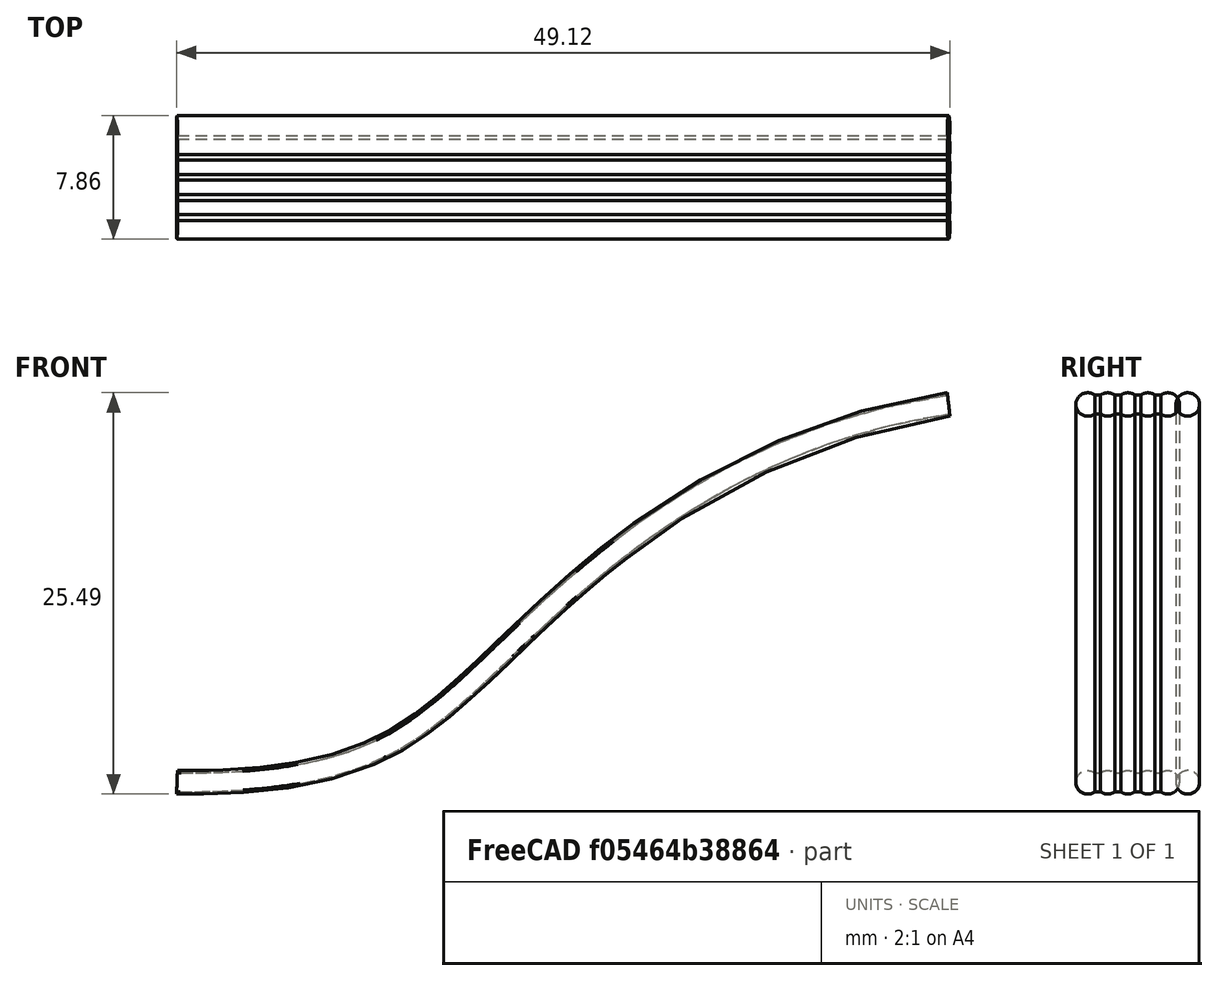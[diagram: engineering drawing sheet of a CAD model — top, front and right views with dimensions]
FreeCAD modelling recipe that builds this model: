
FCSTD DOCUMENT  (FreeCAD 0.20R29603 (Git))
Label: idc
License: All rights reserved
LicenseURL: https://en.wikipedia.org/wiki/All_rights_reserved
objects: Sketcher::SketchObject×4, Part::Sweep×2, App::VRMLObject×2, App::Part×2
note: 6 computed .brp shape members not serialized (recipe doc carries the construction recipe); baked Part::Feature solids carry a one-line shape summary decoded from their .brp

FEATURE [Sketcher::SketchObject] Sketch003
  FullyConstrained = false
  MapMode = 5
  Placement = pos=(0,0,0) rot=(1,0,0;1.5708rad)
  sketch-geometry (11):
    g0-g5: Circle x6 (B-spline internal-alignment scaffolding for g6; pole/knot coordinates omitted)
    g6: BSplineCurve PolesCount=6 KnotsCount=4 Degree=3 IsPeriodic=0
    g7-g10: GeomPoint x4 (B-spline internal-alignment scaffolding for g6; pole/knot coordinates omitted)
  constraints (11):
    c: Weight(g0) = 1
    c: PointOnObject(g6,g-1)
    c: Equal(g0,g1)
    c: PointOnObject(g1,g-2)
    c: Equal(g0,g2)
    c: PointOnObject(g2,g-1)
    c: Equal(g0,g3)
    c: Equal(g0,g4)
    c: Equal(g0,g5)
    c: InternalAlignment(g0-g5 -> g6) x6
    c: InternalAlignment(g7-g10 -> g6) x4
FEATURE [Sketcher::SketchObject] Sketch
  FullyConstrained = false
  MapMode = 5
  Placement = pos=(0,0,0) rot=(0.57735,0.57735,0.57735;2.0944rad)
  sketch-geometry (23):
    g0: LineSegment StartX=0 StartY=0 StartZ=0 EndX=1.27335 EndY=0 EndZ=0
    g1: LineSegment StartX=0 StartY=0 StartZ=0 EndX=1.27103 EndY=0 EndZ=0
    g2: LineSegment StartX=1.27103 StartY=0 StartZ=0 EndX=2.54207 EndY=0 EndZ=0
    g3: LineSegment StartX=2.54207 StartY=0 StartZ=0 EndX=3.8131 EndY=0 EndZ=0
    g4: LineSegment StartX=3.8131 StartY=0 StartZ=0 EndX=5.08414 EndY=0 EndZ=0
    g5: LineSegment StartX=0.45 StartY=0.6 StartZ=0 EndX=0.821034 EndY=0.6 EndZ=0
    g6: LineSegment StartX=0.45 StartY=-0.6 StartZ=0 EndX=0.821034 EndY=-0.6 EndZ=0
    g7: ArcOfCircle CenterX=5.08414 CenterY=7.1e-15 CenterZ=0 NormalX=0 NormalY=0 NormalZ=1 AngleXU=0 Radius=0.75 StartAngle=4.06889 EndAngle=5.35589
    g8: ArcOfCircle CenterX=3.8131 CenterY=0 CenterZ=0 NormalX=0 NormalY=0 NormalZ=1 AngleXU=0 Radius=0.75 StartAngle=4.06889 EndAngle=5.35589
    g9: ArcOfCircle CenterX=2.54207 CenterY=0 CenterZ=0 NormalX=0 NormalY=0 NormalZ=1 AngleXU=0 Radius=0.75 StartAngle=4.06889 EndAngle=5.35589
    g10: ArcOfCircle CenterX=1.27103 CenterY=-2e-16 CenterZ=0 NormalX=0 NormalY=0 NormalZ=1 AngleXU=0 Radius=0.75 StartAngle=4.06889 EndAngle=5.35589
    g11: ArcOfCircle CenterX=0 CenterY=-1e-16 CenterZ=0 NormalX=0 NormalY=0 NormalZ=1 AngleXU=0 Radius=0.75 StartAngle=0.927295 EndAngle=5.35589
    g12: ArcOfCircle CenterX=1.27103 CenterY=0 CenterZ=0 NormalX=0 NormalY=0 NormalZ=1 AngleXU=0 Radius=0.75 StartAngle=0.927295 EndAngle=2.2143
    g13: ArcOfCircle CenterX=2.54207 CenterY=0 CenterZ=0 NormalX=0 NormalY=0 NormalZ=1 AngleXU=0 Radius=0.75 StartAngle=0.927295 EndAngle=2.2143
    g14: ArcOfCircle CenterX=3.8131 CenterY=0 CenterZ=0 NormalX=0 NormalY=0 NormalZ=1 AngleXU=0 Radius=0.75 StartAngle=0.927295 EndAngle=2.2143
    g15: ArcOfCircle CenterX=5.08414 CenterY=-9.81007e-08 CenterZ=0 NormalX=0 NormalY=0 NormalZ=1 AngleXU=0 Radius=0.75 StartAngle=0.927295 EndAngle=2.2143
    g16: LineSegment StartX=4.2631 StartY=0.6 StartZ=0 EndX=4.63414 EndY=0.6 EndZ=0
    g17: LineSegment StartX=2.99207 StartY=0.6 StartZ=0 EndX=3.3631 EndY=0.6 EndZ=0
    g18: LineSegment StartX=1.72103 StartY=0.6 StartZ=0 EndX=2.09207 EndY=0.6 EndZ=0
    g19: LineSegment StartX=1.72103 StartY=-0.6 StartZ=0 EndX=2.09207 EndY=-0.6 EndZ=0
    g20: LineSegment StartX=2.99207 StartY=-0.6 StartZ=0 EndX=3.3631 EndY=-0.6 EndZ=0
    g21: LineSegment StartX=4.2631 StartY=-0.6 StartZ=0 EndX=4.63414 EndY=-0.6 EndZ=0
    g22: ArcOfCircle CenterX=5.08414 CenterY=7.1e-15 CenterZ=0 NormalX=0 NormalY=0 NormalZ=1 AngleXU=0 Radius=0.75 StartAngle=5.35589 EndAngle=7.21048
  constraints (36):
    c: Angle(g0) = 0
    c: Distance(g1) = 1.27103
    c: Angle(g1) = 0
    c: Equal(g1,g2)
    c: Parallel(g2,g1)
    c: Equal(g1,g3)
    c: Parallel(g3,g1)
    c: Equal(g1,g4)
    c: Parallel(g4,g1)
    c: Horizontal(g5)
    c: Horizontal(g6)
    c: PointOnObject(g7,g6)
    c: PointOnObject(g7,g6)
    c: PointOnObject(g8,g6)
    c: PointOnObject(g8,g6)
    c: PointOnObject(g9,g6)
    c: PointOnObject(g9,g6)
    c: Coincident(g6,g11)
    c: Coincident(g11,g5)
    c: Coincident(g16,g15)
    c: Coincident(g17,g14)
    c: Coincident(g16,g14)
    c: Coincident(g18,g13)
    c: Coincident(g17,g13)
    c: Coincident(g5,g12)
    c: Coincident(g18,g12)
    c: Coincident(g6,g10)
    c: Coincident(g19,g10)
    c: PointOnObject(g19,g9)
    c: PointOnObject(g20,g9)
    c: PointOnObject(g20,g8)
    c: PointOnObject(g21,g8)
    c: PointOnObject(g21,g7)
    c: Coincident(g22,g7)
    c: Coincident(g22,g15)
    c: Coincident(g22,g7)
FEATURE [Part::Sweep] Sweep
  Frenet = false
  Sections = -> [Sketch]
  Solid = false
  Spine = -> Sketch003 [Edge1]
  Transition = 1
FEATURE [App::VRMLObject] _90157000672001  label="690157000672001"
FEATURE [App::Part] Part
  Group = -> [_90157000672001]
  Origin = -> Origin
  Placement = pos=(-1.5e-15,3.25,0.5) rot=(0.707107,0.707107,0;3.14159rad)
FEATURE [Sketcher::SketchObject] Sketch005
  FullyConstrained = false
  MapMode = 5
  Placement = pos=(0,0,0) rot=(0.57735,0.57735,0.57735;2.0944rad)
  sketch-geometry (2):
    g0: ArcOfCircle CenterX=6.35517 CenterY=-2.69756e-08 CenterZ=0 NormalX=0 NormalY=0 NormalZ=1 AngleXU=0 Radius=0.75 StartAngle=4.06889 EndAngle=8.49748
    g1: ArcOfCircle CenterX=6.35517 CenterY=-2.69756e-08 CenterZ=0 NormalX=0 NormalY=0 NormalZ=1 AngleXU=0 Radius=0.75 StartAngle=2.2143 EndAngle=4.06889
  constraints (4):
    c: Radius(g0) = 0.75
    c: Coincident(g1,g0)
    c: Coincident(g1,g0)
    c: Coincident(g1,g0)
FEATURE [Sketcher::SketchObject] Sketch006
  FullyConstrained = false
  MapMode = 5
  Placement = pos=(0,0,0) rot=(1,0,0;1.5708rad)
  sketch-geometry (11):
    g0-g5: Circle x6 (B-spline internal-alignment scaffolding for g6; pole/knot coordinates omitted)
    g6: BSplineCurve PolesCount=6 KnotsCount=4 Degree=3 IsPeriodic=0
    g7-g10: GeomPoint x4 (B-spline internal-alignment scaffolding for g6; pole/knot coordinates omitted)
  constraints (11):
    c: Weight(g0) = 1
    c: PointOnObject(g6,g-1)
    c: Equal(g0,g1)
    c: PointOnObject(g1,g-2)
    c: Equal(g0,g2)
    c: PointOnObject(g2,g-1)
    c: Equal(g0,g3)
    c: Equal(g0,g4)
    c: Equal(g0,g5)
    c: InternalAlignment(g0-g5 -> g6) x6
    c: InternalAlignment(g7-g10 -> g6) x4
FEATURE [Part::Sweep] Sweep001
  Frenet = false
  Sections = -> [Sketch005]
  Solid = false
  Spine = -> Sketch006 [Edge1]
  Transition = 1
FEATURE [App::VRMLObject] _90157000672002  label="690157000672001001"
FEATURE [App::Part] Part001
  Group = -> [_90157000672002]
  Origin = -> Origin001
  Placement = pos=(43,3.25,23.5) rot=(-0.704063,-0.704063,-0.092692;3.32645rad)
